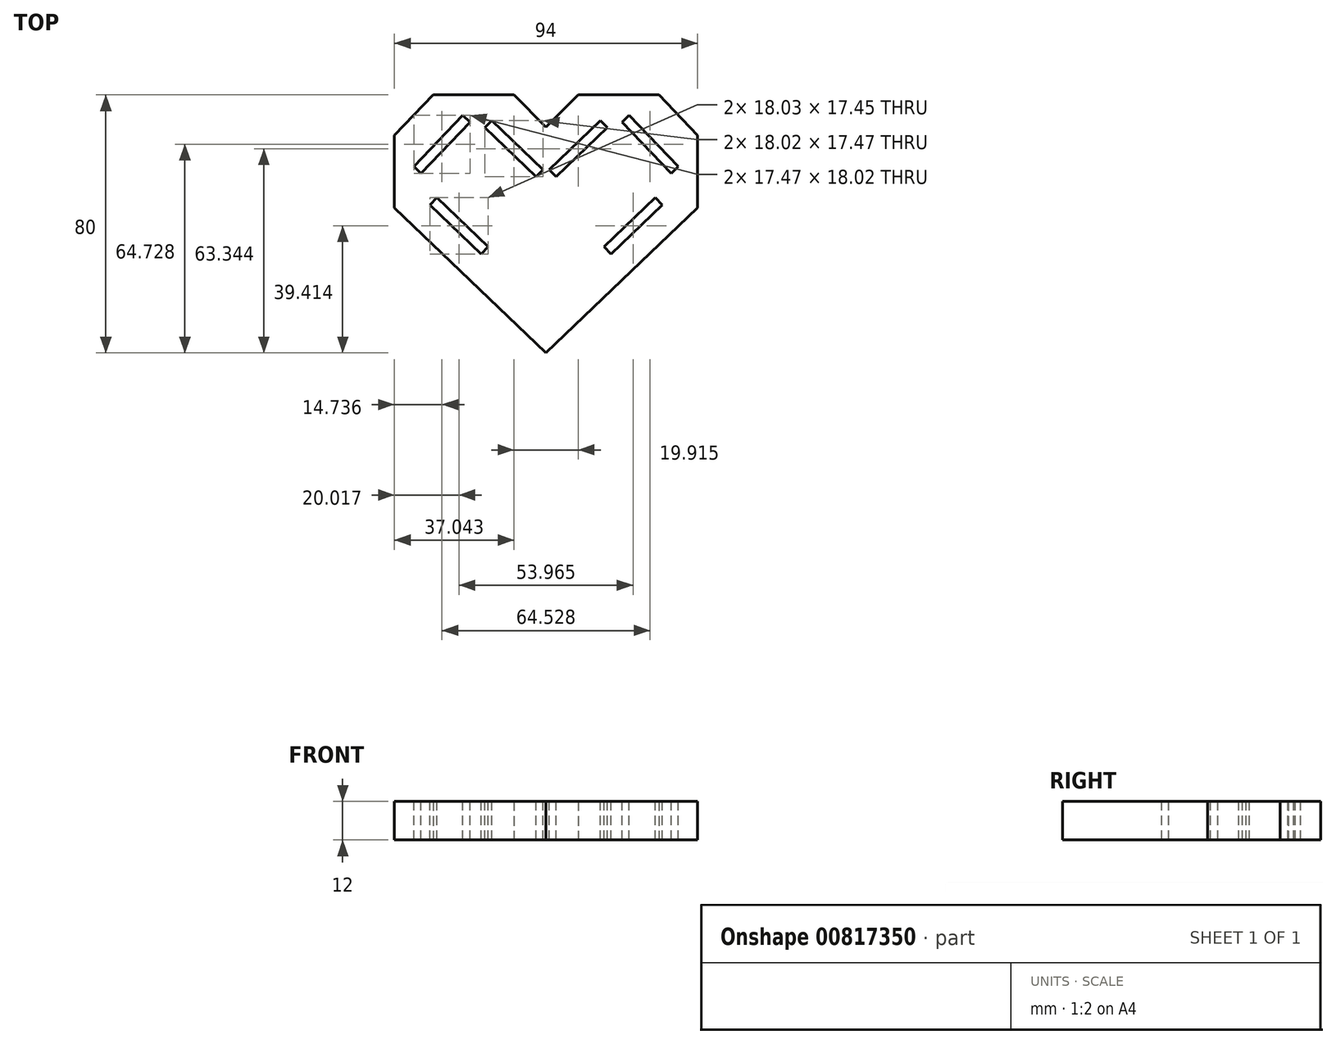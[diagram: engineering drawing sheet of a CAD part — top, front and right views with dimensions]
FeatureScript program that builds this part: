
annotation { "Feature Type Name" : "Feature", "Feature Type Description" : "" }
export const myFeature = defineFeature(function(context is Context, id is Id, definition is map)
    precondition{}
    {
        {
            var Q0;
            Q0=qCreatedBy(makeId("Top.planeOp"),FACE);
            var sketch = newSketch(context, id + "F0", { "sketchPlane" : qUnion([Q0])});
            skLineSegment(sketch, "E0", {"start": v(0, -61) * mm, "end": v(47, -16) * mm});
            skLineSegment(sketch, "E1", {"start": v(47, -16) * mm, "end": v(47, 6.5) * mm});
            skLineSegment(sketch, "E2", {"start": v(47, 6.5) * mm, "end": v(35, 19) * mm});
            skLineSegment(sketch, "E3", {"start": v(35, 19) * mm, "end": v(10, 19) * mm});
            skLineSegment(sketch, "E4", {"start": v(10, 19) * mm, "end": v(0, 9) * mm});
            skLineSegment(sketch, "E5.MirrorCS", {"start": v(-10, 19) * mm, "end": v(0, 9) * mm});
            skLineSegment(sketch, "E6.MirrorCS", {"start": v(-35, 19) * mm, "end": v(-10, 19) * mm});
            skLineSegment(sketch, "E7.MirrorCS", {"start": v(-47, 6.5) * mm, "end": v(-35, 19) * mm});
            skLineSegment(sketch, "E8.MirrorCS", {"start": v(-47, -16) * mm, "end": v(-47, 6.5) * mm});
            skLineSegment(sketch, "E9.MirrorCS", {"start": v(0, -61) * mm, "end": v(-47, -16) * mm});
            skSolve(sketch);
        }
        {
            var Q0;
            Q0=qSketchRegion(id+"F0",true);
            extrude(context, id + "F1", {"entities" : qUnion([Q0]), "depth" : 12 * mm, "offsetDistance" : 25 * mm});
        }
        {
            var Q0;
            Q0=makeQuery(id+"F1.opExtrude","CAP_FACE",FACE,{"disambiguationData":[OSD([sQuery(id+"F0.wireOp",EDGE,"E0"),sQuery(id+"F0.wireOp",EDGE,"E1"),sQuery(id+"F0.wireOp",EDGE,"E2"),sQuery(id+"F0.wireOp",EDGE,"E3"),sQuery(id+"F0.wireOp",EDGE,"E4"),sQuery(id+"F0.wireOp",EDGE,"82c20e4c-a16d-44ab-ba3a-01f44a2a79d4.MirrorCS"),sQuery(id+"F0.wireOp",EDGE,"ec838d24-a44d-4492-aded-78a89141ed91.MirrorCS"),sQuery(id+"F0.wireOp",EDGE,"bd7d52e1-2083-4ff2-afdd-3f343d5251aa.MirrorCS"),sQuery(id+"F0.wireOp",EDGE,"4fc21238-a6f4-42ad-b0c3-35517250600e.MirrorCS"),sQuery(id+"F0.wireOp",EDGE,"0c5398ae-afa2-41ec-94e7-8fb47a1d7522.MirrorCS")])],"isStart":false});
            var sketch = newSketch(context, id + "F2", { "sketchPlane" : qUnion([Q0])});
            skLineSegment(sketch, "E10", {"start": v(41, -3.13) * mm, "end": v(25.76, 12.74) * mm});
            skLineSegment(sketch, "E11", {"start": v(41, -3.13) * mm, "end": v(38.76, -5.28) * mm});
            skLineSegment(sketch, "E12", {"start": v(38.76, -5.28) * mm, "end": v(23.53, 10.59) * mm});
            skLineSegment(sketch, "E13", {"start": v(23.53, 10.59) * mm, "end": v(25.76, 12.74) * mm});
            skLineSegment(sketch, "E14.MirrorCS", {"start": v(-23.53, 10.59) * mm, "end": v(-25.76, 12.74) * mm});
            skLineSegment(sketch, "E15.MirrorCS", {"start": v(-41, -3.13) * mm, "end": v(-25.76, 12.74) * mm});
            skLineSegment(sketch, "E16.MirrorCS", {"start": v(-38.76, -5.28) * mm, "end": v(-23.53, 10.59) * mm});
            skLineSegment(sketch, "E17.MirrorCS", {"start": v(-41, -3.13) * mm, "end": v(-38.76, -5.28) * mm});
            skLineSegment(sketch, "E18", {"start": v(18.97, 8.84) * mm, "end": v(3.1, -6.4) * mm});
            skLineSegment(sketch, "E19", {"start": v(3.1, -6.4) * mm, "end": v(0.95, -4.16) * mm});
            skLineSegment(sketch, "E20", {"start": v(0.95, -4.16) * mm, "end": v(16.82, 11.08) * mm});
            skLineSegment(sketch, "E21", {"start": v(16.82, 11.08) * mm, "end": v(18.97, 8.84) * mm});
            skLineSegment(sketch, "E22", {"start": v(-11, -42.16) * mm, "end": v(11, -42.16) * mm});
            skLineSegment(sketch, "E23", {"start": v(11, -42.16) * mm, "end": v(-11, -42.16) * mm});
            skLineSegment(sketch, "E24", {"start": v(-11, -39.06) * mm, "end": v(-11, -42.16) * mm});
            skLineSegment(sketch, "E25", {"start": v(-11, -39.06) * mm, "end": v(11, -39.06) * mm});
            skLineSegment(sketch, "E26", {"start": v(11, -39.06) * mm, "end": v(11, -42.16) * mm});
            skPoint(sketch, "E27.start.orphan", {"position": v(17.97, -28.07) * mm});
            skPoint(sketch, "E28.start.orphan", {"position": v(20.1, -30.31) * mm});
            skPoint(sketch, "E29.end.orphan", {"position": v(36, -15.1) * mm});
            skPoint(sketch, "E29.start.orphan", {"position": v(33.86, -12.86) * mm});
            skLineSegment(sketch, "E30", {"start": v(20.1, -30.31) * mm, "end": v(36, -15.1) * mm});
            skLineSegment(sketch, "E31", {"start": v(33.86, -12.86) * mm, "end": v(36, -15.1) * mm});
            skLineSegment(sketch, "E32", {"start": v(33.86, -12.86) * mm, "end": v(17.97, -28.07) * mm});
            skLineSegment(sketch, "E33", {"start": v(17.97, -28.07) * mm, "end": v(20.1, -30.31) * mm});
            skPoint(sketch, "E34.MirrorCS.end.orphan", {"position": v(-17.97, -28.07) * mm});
            skPoint(sketch, "E34.MirrorCS.start.orphan", {"position": v(-20.1, -30.31) * mm});
            skPoint(sketch, "E35.MirrorCS.end.orphan", {"position": v(-33.86, -12.86) * mm});
            skPoint(sketch, "E36.MirrorCS.end.orphan", {"position": v(-36, -15.1) * mm});
            skLineSegment(sketch, "E37.MirrorCS", {"start": v(-33.86, -12.86) * mm, "end": v(-17.97, -28.07) * mm});
            skLineSegment(sketch, "E38.MirrorCS", {"start": v(-20.1, -30.31) * mm, "end": v(-36, -15.1) * mm});
            skLineSegment(sketch, "E39.MirrorCS", {"start": v(-17.97, -28.07) * mm, "end": v(-20.1, -30.31) * mm});
            skLineSegment(sketch, "E40.MirrorCS", {"start": v(-33.86, -12.86) * mm, "end": v(-36, -15.1) * mm});
            skLineSegment(sketch, "E41.MirrorCS", {"start": v(-3.1, -6.4) * mm, "end": v(-0.95, -4.16) * mm});
            skLineSegment(sketch, "E42.MirrorCS", {"start": v(-0.95, -4.16) * mm, "end": v(-16.82, 11.08) * mm});
            skLineSegment(sketch, "E43.MirrorCS", {"start": v(-18.97, 8.84) * mm, "end": v(-3.1, -6.4) * mm});
            skLineSegment(sketch, "E44.MirrorCS", {"start": v(-16.82, 11.08) * mm, "end": v(-18.97, 8.84) * mm});
            skSolve(sketch);
        }
        {
            var Q0;
            Q0=makeQuery(id+"F2.imprint","IMPRINT",FACE,{"disambiguationData":[TD([[makeQuery(id+"F2.imprint","IMPRINT",EDGE,{"derivedFrom":sQuery(id+"F2.wireOp",EDGE,"E10")}),1.0]])]});
            var Q1;
            Q1=makeQuery(id+"F2.imprint","IMPRINT",FACE,{"disambiguationData":[TD([[makeQuery(id+"F2.imprint","IMPRINT",EDGE,{"derivedFrom":sQuery(id+"F2.wireOp",EDGE,"E30")}),1.0]])]});
            var Q2;
            Q2=makeQuery(id+"F2.imprint","IMPRINT",FACE,{"disambiguationData":[TD([[makeQuery(id+"F2.imprint","IMPRINT",EDGE,{"derivedFrom":sQuery(id+"F2.wireOp",EDGE,"E23")}),-1.0]])]});
            var Q3;
            Q3=makeQuery(id+"F2.imprint","IMPRINT",FACE,{"disambiguationData":[TD([[makeQuery(id+"F2.imprint","IMPRINT",EDGE,{"derivedFrom":sQuery(id+"F2.wireOp",EDGE,"E37.MirrorCS")}),-1.0]])]});
            var Q4;
            Q4=makeQuery(id+"F2.imprint","IMPRINT",FACE,{"disambiguationData":[TD([[makeQuery(id+"F2.imprint","IMPRINT",EDGE,{"derivedFrom":sQuery(id+"F2.wireOp",EDGE,"E18")}),-1.0]])]});
            var Q5;
            Q5=makeQuery(id+"F2.imprint","IMPRINT",FACE,{"disambiguationData":[TD([[makeQuery(id+"F2.imprint","IMPRINT",EDGE,{"derivedFrom":sQuery(id+"F2.wireOp",EDGE,"E41.MirrorCS")}),1.0]])]});
            var Q6;
            Q6=makeQuery(id+"F2.imprint","IMPRINT",FACE,{"disambiguationData":[TD([[makeQuery(id+"F2.imprint","IMPRINT",EDGE,{"derivedFrom":sQuery(id+"F2.wireOp",EDGE,"E14.MirrorCS")}),1.0]])]});
            extrude(context, id + "F3", {"entities" : qUnion([Q0, Q1, Q2, Q3, Q4, Q5, Q6]), "operationType" : NewBodyOperationType.REMOVE, "oppositeDirection" : true, "depth" : 25 * mm, "offsetDistance" : 25 * mm});
        }
    });
